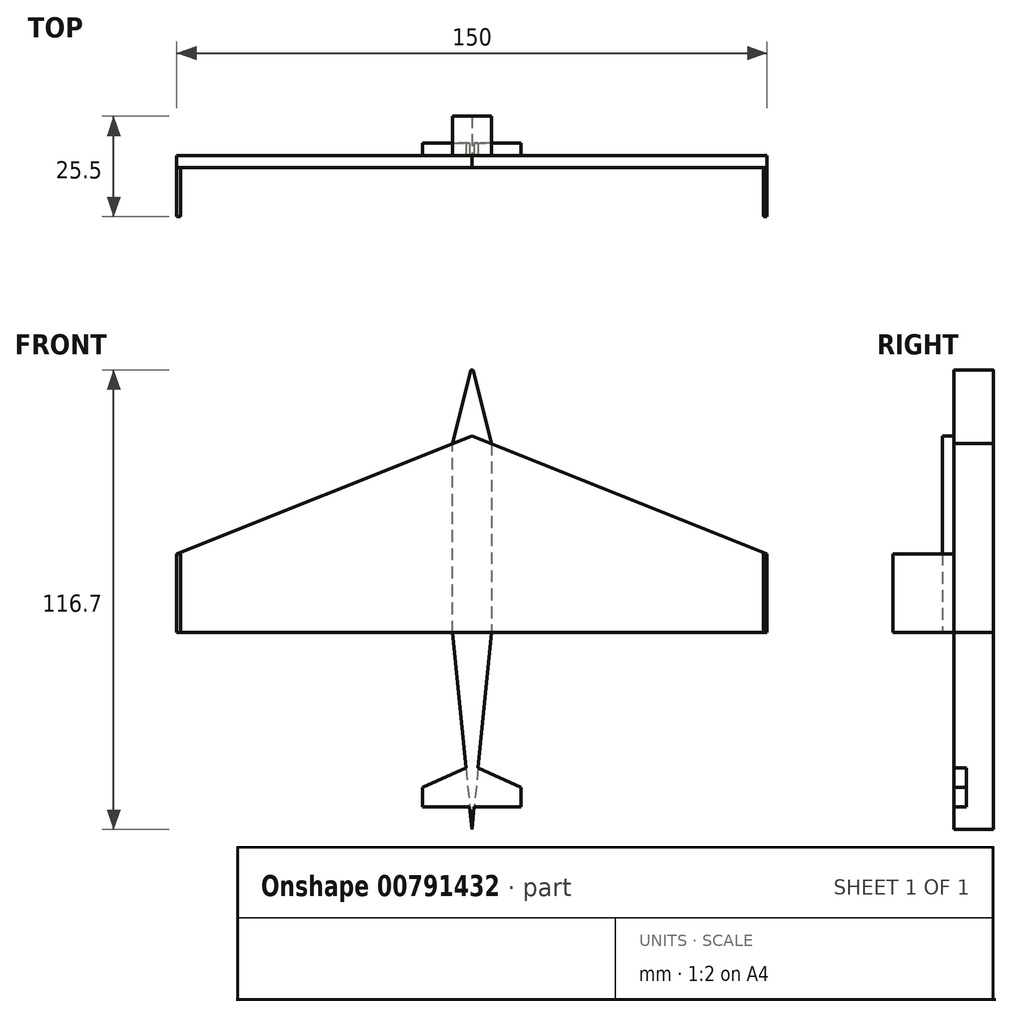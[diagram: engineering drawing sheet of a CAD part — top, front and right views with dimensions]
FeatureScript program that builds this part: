
annotation { "Feature Type Name" : "Feature", "Feature Type Description" : "" }
export const myFeature = defineFeature(function(context is Context, id is Id, definition is map)
    precondition{}
    {
        {
            var Q0;
            Q0=qCreatedBy(makeId("Front.planeOp"),FACE);
            var sketch = newSketch(context, id + "F0", { "sketchPlane" : qUnion([Q0])});
            skLineSegment(sketch, "E0", {"start": v(-75, 24.43) * mm, "end": v(-75, 4.43) * mm});
            skLineSegment(sketch, "E1", {"start": v(-75, 4.43) * mm, "end": v(75, 4.43) * mm});
            skLineSegment(sketch, "E2", {"start": v(75, 4.43) * mm, "end": v(75, 24.43) * mm});
            skLineSegment(sketch, "E3", {"start": v(75, 4.43) * mm, "end": v(75, -7.92) * mm, "construction": true});
            skLineSegment(sketch, "E4", {"start": v(75, -7.92) * mm, "end": v(0, -7.92) * mm, "construction": true});
            skLineSegment(sketch, "E5", {"start": v(0, 4.43) * mm, "end": v(0, 54.43) * mm});
            skLineSegment(sketch, "E6", {"start": v(-75, 24.43) * mm, "end": v(0, 54.43) * mm});
            skLineSegment(sketch, "E7", {"start": v(75, 24.43) * mm, "end": v(0, 54.43) * mm});
            skSolve(sketch);
        }
        {
            var Q0;
            {var subQ0=sQuery(id+"F0.wireOp",EDGE,"E0");Q0=makeQuery(id+"F0.imprint","IMPRINT",FACE,{"disambiguationData":[TD([[makeQuery(id+"F0.imprint","IMPRINT",EDGE,{"derivedFrom":subQ0}),1.0]])]});}
            var Q1;
            {var subQ0=sQuery(id+"F0.wireOp",EDGE,"E2");Q1=makeQuery(id+"F0.imprint","IMPRINT",FACE,{"disambiguationData":[TD([[makeQuery(id+"F0.imprint","IMPRINT",EDGE,{"derivedFrom":subQ0}),1.0]])]});}
            extrude(context, id + "F1", {"entities" : qUnion([Q0, Q1]), "depth" : 3 * mm, "hasOffset" : true, "offsetDistance" : 25 * mm});
        }
        {
            var Q0;
            Q0=makeQuery(id+"F1.opExtrude","CAP_FACE",FACE,{"disambiguationData":[OSD([sQuery(id+"F0.wireOp",EDGE,"E0"),sQuery(id+"F0.wireOp",EDGE,"E1"),sQuery(id+"F0.wireOp",EDGE,"E2"),sQuery(id+"F0.wireOp",EDGE,"E6"),sQuery(id+"F0.wireOp",EDGE,"E7")])],"isStart":false});
            var sketch = newSketch(context, id + "F2", { "sketchPlane" : qUnion([Q0])});
            skLineSegment(sketch, "E8.bottom", {"start": v(-75, 24.43) * mm, "end": v(-74, 24.43) * mm});
            skLineSegment(sketch, "E8.top", {"start": v(-75, 4.43) * mm, "end": v(-74, 4.43) * mm});
            skLineSegment(sketch, "E8.left", {"start": v(-75, 24.43) * mm, "end": v(-75, 4.43) * mm});
            skLineSegment(sketch, "E8.right", {"start": v(-74, 24.43) * mm, "end": v(-74, 4.43) * mm});
            skLineSegment(sketch, "E9.bottom", {"start": v(75, 24.43) * mm, "end": v(74, 24.43) * mm});
            skLineSegment(sketch, "E9.top", {"start": v(75, 4.43) * mm, "end": v(74, 4.43) * mm});
            skLineSegment(sketch, "E9.left", {"start": v(75, 24.43) * mm, "end": v(75, 4.43) * mm});
            skLineSegment(sketch, "E9.right", {"start": v(74, 24.43) * mm, "end": v(74, 4.43) * mm});
            skSolve(sketch);
        }
        {
            var Q0;
            Q0=makeQuery(id+"F2.imprint","IMPRINT",FACE,{"disambiguationData":[TD([[makeQuery(id+"F2.imprint","IMPRINT",EDGE,{"derivedFrom":sQuery(id+"F2.wireOp",EDGE,"E8.bottom")}),-1.0]])]});
            var Q1;
            Q1=makeQuery(id+"F2.imprint","IMPRINT",FACE,{"disambiguationData":[TD([[makeQuery(id+"F2.imprint","IMPRINT",EDGE,{"derivedFrom":sQuery(id+"F2.wireOp",EDGE,"E9.bottom")}),1.0]])]});
            extrude(context, id + "F3", {"entities" : qUnion([Q0, Q1]), "operationType" : NewBodyOperationType.ADD, "depth" : 12.5 * mm, "offsetDistance" : 25 * mm});
        }
        {
            var Q0;
            Q0=makeQuery(id+"F1.opExtrude","CAP_FACE",FACE,{"disambiguationData":[OSD([sQuery(id+"F0.wireOp",EDGE,"E0"),sQuery(id+"F0.wireOp",EDGE,"E1"),sQuery(id+"F0.wireOp",EDGE,"E2"),sQuery(id+"F0.wireOp",EDGE,"E6"),sQuery(id+"F0.wireOp",EDGE,"E7")])],"isStart":true});
            var sketch = newSketch(context, id + "F4", { "sketchPlane" : qUnion([Q0])});
            skLineSegment(sketch, "E10", {"start": v(0, 0) * mm, "end": v(0, 54.43) * mm, "construction": true});
            skLineSegment(sketch, "E11", {"start": v(0, 54.43) * mm, "end": v(47.63, 35.38) * mm, "construction": true});
            skLineSegment(sketch, "E12", {"start": v(0, 54.43) * mm, "end": v(-40.71, 38.14) * mm, "construction": true});
            skLineSegment(sketch, "E13", {"start": v(-48.2, 4.43) * mm, "end": v(58.2, 4.43) * mm, "construction": true});
            skLineSegment(sketch, "E14", {"start": v(0, 4.43) * mm, "end": v(5, 4.43) * mm});
            skLineSegment(sketch, "E15", {"start": v(5, 4.43) * mm, "end": v(5, 52.43) * mm});
            skLineSegment(sketch, "E16", {"start": v(5, 52.43) * mm, "end": v(-5, 52.43) * mm});
            skLineSegment(sketch, "E17", {"start": v(-5, 52.43) * mm, "end": v(-5, 4.43) * mm});
            skLineSegment(sketch, "E18", {"start": v(-5, 4.43) * mm, "end": v(0, 4.43) * mm});
            skLineSegment(sketch, "E19", {"start": v(0, 52.43) * mm, "end": v(0, 72.43) * mm});
            skLineSegment(sketch, "E20", {"start": v(0, 4.43) * mm, "end": v(0, -45.57) * mm});
            skLineSegment(sketch, "E21", {"start": v(-5, 52.43) * mm, "end": v(0, 72.43) * mm});
            skLineSegment(sketch, "E22", {"start": v(5, 52.43) * mm, "end": v(0, 72.43) * mm});
            skLineSegment(sketch, "E23", {"start": v(-5, 4.43) * mm, "end": v(0, -45.57) * mm});
            skLineSegment(sketch, "E24", {"start": v(5, 4.43) * mm, "end": v(0, -45.57) * mm});
            skSolve(sketch);
        }
        {
            var Q0;
            Q0=makeQuery(id+"F4.imprint","IMPRINT",FACE,{"disambiguationData":[TD([[makeQuery(id+"F4.imprint","IMPRINT",EDGE,{"derivedFrom":sQuery(id+"F4.wireOp",EDGE,"E14")}),-1.0]])]});
            extrude(context, id + "F5", {"entities" : qUnion([Q0]), "operationType" : NewBodyOperationType.ADD, "depth" : 10 * mm, "offsetDistance" : 25 * mm});
        }
        {
            var Q0;
            Q0 = qSketchRegion(id + "F4", true);
            extrude(context, id + "F6", {"entities" : qUnion([Q0]), "operationType" : NewBodyOperationType.ADD, "depth" : 10 * mm, "offsetDistance" : 25 * mm});
        }
        {
            var Q0;
            {var subQ0=sQuery(id+"F4.wireOp",EDGE,"E24");var subQ1=sQuery(id+"F0.wireOp",EDGE,"E1");var subQ2=sQuery(id+"F4.wireOp",EDGE,"E15");var subQ3=sQuery(id+"F4.wireOp",EDGE,"E23");var subQ4=sQuery(id+"F4.wireOp",EDGE,"E17");Q0=makeQuery(id+"F6.boolean.opBoolean","SPLIT",FACE,{"disambiguationData":[TD([makeQuery(id+"F1.opExtrude","SWEPT_FACE",FACE,{"disambiguationData":[OSD([subQ1])]})])],"derivedFrom":makeQuery(id+"F6.opExtrude","CAP_FACE",FACE,{"disambiguationData":[OSD([subQ2,subQ4,sQuery(id+"F4.wireOp",EDGE,"E21"),sQuery(id+"F4.wireOp",EDGE,"E22"),subQ3,subQ0])],"isStart":true})});}
            var sketch = newSketch(context, id + "F7", { "sketchPlane" : qUnion([Q0])});
            skLineSegment(sketch, "E25", {"start": v(0, -45.57) * mm, "end": v(0, 0) * mm, "construction": true});
            skLineSegment(sketch, "E26", {"start": v(0, -39.85) * mm, "end": v(12.5, -39.85) * mm});
            skLineSegment(sketch, "E27", {"start": v(0, -39.85) * mm, "end": v(-12.5, -39.85) * mm});
            skLineSegment(sketch, "E28", {"start": v(-12.5, -39.85) * mm, "end": v(-12.5, -34.85) * mm});
            skLineSegment(sketch, "E29", {"start": v(-12.5, -34.85) * mm, "end": v(0, -29.28) * mm});
            skLineSegment(sketch, "E30", {"start": v(12.5, -39.85) * mm, "end": v(12.5, -34.85) * mm});
            skLineSegment(sketch, "E31", {"start": v(12.5, -34.85) * mm, "end": v(0, -29.28) * mm});
            skSolve(sketch);
        }
        {
            var Q0;
            {var subQ0=sQuery(id+"F7.wireOp",EDGE,"E28");Q0=makeQuery(id+"F7.imprint","IMPRINT",FACE,{"disambiguationData":[TD([[makeQuery(id+"F7.imprint","IMPRINT",EDGE,{"derivedFrom":subQ0}),-1.0]])]});}
            var Q1;
            {var subQ0=sQuery(id+"F7.wireOp",EDGE,"E30");Q1=makeQuery(id+"F7.imprint","IMPRINT",FACE,{"disambiguationData":[TD([[makeQuery(id+"F7.imprint","IMPRINT",EDGE,{"derivedFrom":subQ0}),1.0]])]});}
            extrude(context, id + "F8", {"entities" : qUnion([Q0, Q1]), "operationType" : NewBodyOperationType.ADD, "oppositeDirection" : true, "depth" : 3.1 * mm, "offsetDistance" : 25 * mm});
        }
        {
            var Q0;
            Q0=makeQuery(id+"F6.opExtrude","SWEPT_EDGE",EDGE,{"disambiguationData":[OSD([sQuery(id+"F4.wireOp",EDGE,"E19"),sQuery(id+"F4.wireOp",EDGE,"E21"),sQuery(id+"F4.wireOp",EDGE,"E22")])]});
            fillet(context, id + "F9", {"entities" : qUnion([Q0]), "radius" : 0.42 * mm, "tangentPropagation" : true, "allowEdgeOverflow" : false});
        }
    });
